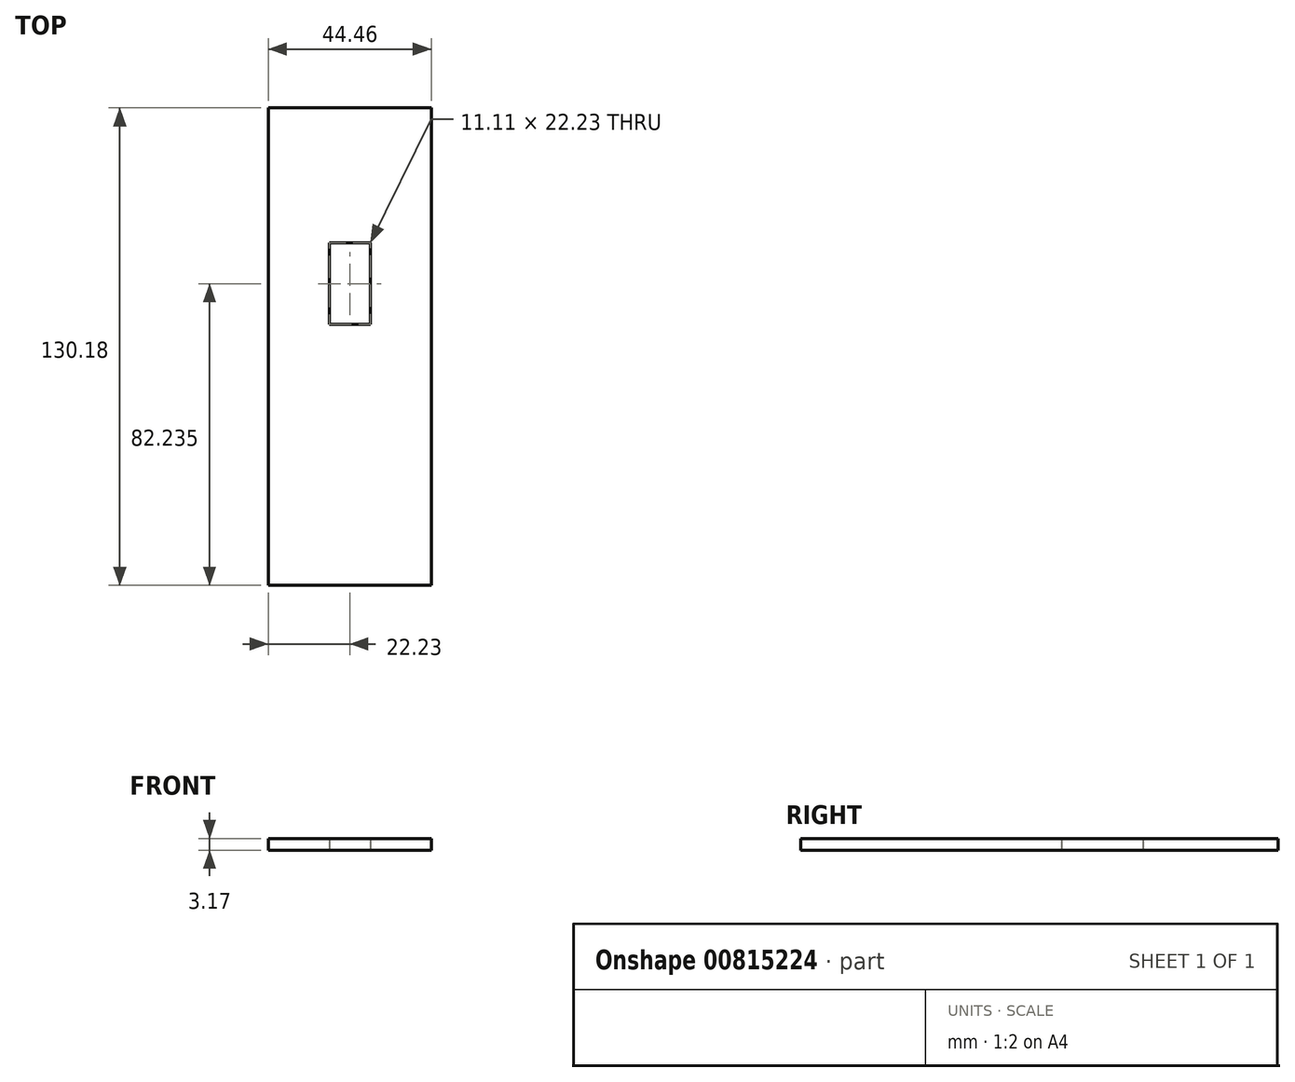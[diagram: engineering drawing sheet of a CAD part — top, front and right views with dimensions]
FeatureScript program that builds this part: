
annotation { "Feature Type Name" : "Feature", "Feature Type Description" : "" }
export const myFeature = defineFeature(function(context is Context, id is Id, definition is map)
    precondition{}
    {
        {
            var Q0;
            Q0=qCreatedBy(makeId("Top.planeOp"),FACE);
            var sketch = newSketch(context, id + "F0", { "sketchPlane" : qUnion([Q0])});
            skLineSegment(sketch, "E0.bottom", {"start": v(22.23, -65.09) * mm, "end": v(-22.23, -65.09) * mm});
            skLineSegment(sketch, "E0.top", {"start": v(22.22, 65.09) * mm, "end": v(-22.23, 65.09) * mm});
            skLineSegment(sketch, "E0.left", {"start": v(22.22, -65.09) * mm, "end": v(22.23, 65.09) * mm});
            skLineSegment(sketch, "E0.right", {"start": v(-22.23, -65.09) * mm, "end": v(-22.23, 65.09) * mm});
            skPoint(sketch, "E0.middle", {"position": v(0, 0) * mm});
            skPoint(sketch, "E1", {"position": v(0, 65.09) * mm});
            skPoint(sketch, "E2", {"position": v(0, -65.09) * mm});
            skLineSegment(sketch, "E3", {"start": v(0, 65.09) * mm, "end": v(0, -65.09) * mm});
            skLineSegment(sketch, "E4.bottom", {"start": v(5.56, 28.26) * mm, "end": v(-5.56, 28.26) * mm});
            skLineSegment(sketch, "E4.top", {"start": v(5.56, 6.03) * mm, "end": v(-5.56, 6.03) * mm});
            skLineSegment(sketch, "E4.left", {"start": v(5.56, 28.26) * mm, "end": v(5.56, 6.03) * mm});
            skLineSegment(sketch, "E4.right", {"start": v(-5.56, 28.26) * mm, "end": v(-5.56, 6.03) * mm});
            skPoint(sketch, "E4.middle", {"position": v(0, 17.15) * mm});
            skSolve(sketch);
        }
        {
            var Q0;
            Q0=makeQuery(id+"F0.imprint","IMPRINT",FACE,{"disambiguationData":[TD([[makeQuery(id+"F0.imprint","IMPRINT",EDGE,{"derivedFrom":sQuery(id+"F0.wireOp",EDGE,"E0.bottom")}),-1.0]])]});
            extrude(context, id + "F1", {"entities" : qUnion([Q0]), "depth" : 3.17 * mm, "offsetDistance" : 25.4 * mm});
        }
    });
